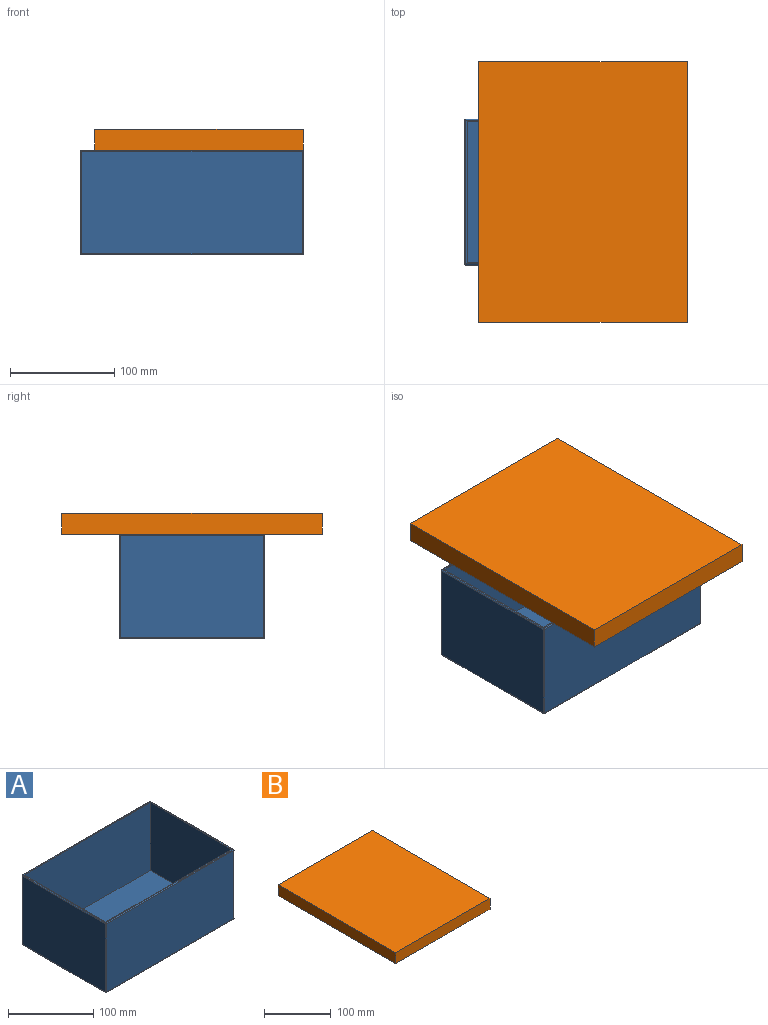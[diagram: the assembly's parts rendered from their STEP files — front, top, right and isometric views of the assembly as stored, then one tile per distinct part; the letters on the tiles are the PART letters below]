
ASSEMBLY  parts=2 mates=2
PART A: 31 faces, bbox 213.3x139.7x100 mm
  f0: plane 211.31x137.65mm, normal (0,0,1), area 900.5mm2, adj f6,f7,f8,f9,f14,f15,f24,f25
  f1: plane 211.31x98mm, normal (0,1,0), area 20708mm2, adj f19,f24,f27,f30
  f2: plane 137.65x98mm, normal (-1,0,0), area 13489.9mm2, adj f16,f25,f26,f30
  f3: plane 211.31x98mm, normal (0,-1,0), area 20708mm2, adj f11,f15,f16,f17
  f4: plane 137.65x98mm, normal (1,0,0), area 13489.9mm2, adj f11,f14,f18,f19
  f5: plane 211.31x137.65mm, normal (0,0,-1), area 29086.7mm2, adj f17,f18,f26,f27
  f6: plane 208.71x97.7mm, normal (0,-1,0), area 20390.6mm2, adj f0,f7,f9,f10
  f7: plane 135.05x97.7mm, normal (1,0,0), area 13194.6mm2, adj f0,f6,f8,f10
  f8: plane 208.71x97.7mm, normal (0,1,0), area 20390.6mm2, adj f0,f7,f9,f10
  f9: plane 135.05x97.7mm, normal (-1,0,0), area 13194.6mm2, adj f0,f6,f8,f10
  f10: plane 208.71x135.05mm, normal (0,0,1), area 28186.2mm2, adj f6,f7,f8,f9
  f11: cylinder r=1mm len=98mm, axis (0,0,1), area 153.9mm2, adj f3,f4,f12,f13
  f12: sphere r=1mm, area 1.6mm2, adj f11,f14,f15
  f13: sphere r=1mm, area 1.6mm2, adj f11,f17,f18
  f14: cylinder r=1mm len=137.65mm, axis (0,-1,0), area 216.2mm2, adj f0,f4,f12,f20
  f15: cylinder r=1mm len=211.31mm, axis (-1,0,0), area 331.9mm2, adj f0,f3,f12,f21
  f16: cylinder r=1mm len=98mm, axis (0,0,-1), area 153.9mm2, adj f2,f3,f21,f22
  f17: cylinder r=1mm len=211.31mm, axis (1,0,0), area 331.9mm2, adj f3,f5,f13,f22
  f18: cylinder r=1mm len=137.65mm, axis (0,1,0), area 216.2mm2, adj f4,f5,f13,f23
  f19: cylinder r=1mm len=98mm, axis (0,0,-1), area 153.9mm2, adj f1,f4,f20,f23
  f20: sphere r=1mm, area 1.6mm2, adj f14,f19,f24
  f21: sphere r=1mm, area 1.6mm2, adj f15,f16,f25
  f22: sphere r=1mm, area 1.6mm2, adj f16,f17,f26
  f23: sphere r=1mm, area 1.6mm2, adj f18,f19,f27
  f24: cylinder r=1mm len=211.31mm, axis (1,0,0), area 331.9mm2, adj f0,f1,f20,f28
  f25: cylinder r=1mm len=137.65mm, axis (0,1,0), area 216.2mm2, adj f0,f2,f21,f28
  f26: cylinder r=1mm len=137.65mm, axis (0,-1,0), area 216.2mm2, adj f2,f5,f22,f29
  f27: cylinder r=1mm len=211.31mm, axis (-1,0,0), area 331.9mm2, adj f1,f5,f23,f29
  f28: sphere r=1mm, area 1.6mm2, adj f24,f25,f30
  f29: sphere r=1mm, area 1.6mm2, adj f26,f27,f30
  f30: cylinder r=1mm len=98mm, axis (0,0,1), area 153.9mm2, adj f1,f2,f28,f29
PART B: 6 faces, bbox 200x250x20 mm
  f0: plane 200x20mm, normal (0,1,0), area 4000mm2, adj f1,f3,f4,f5
  f1: plane 250x20mm, normal (-1,0,0), area 5000mm2, adj f0,f2,f4,f5
  f2: plane 200x20mm, normal (0,-1,0), area 4000mm2, adj f1,f3,f4,f5
  f3: plane 250x20mm, normal (1,0,0), area 5000mm2, adj f0,f2,f4,f5
  f4: plane 250x200mm, normal (0,0,1), area 50000mm2, adj f0,f1,f2,f3
  f5: plane 250x200mm, normal (0,0,-1), area 50000mm2, adj f0,f1,f2,f3
PLACE A t=(133.65,-593.34,585.73)mm fixed
PLACE B t=(2618.72,1950.73,685.73)mm
MATE planar B.f3 <-> A.f4  axis (1,0,0) through (243.02,-605.63,695.73)mm
MATE planar A.f0 <-> B.f5  axis (0,0,1) through (136.37,-605.63,685.73)mm
